# Revit family: Modular Panel_132X
name_source: partatom
category: Electrical Fixtures
revit_build: Autodesk Revit 2018 (Build: 20170223_1515(x64)
units: mm (PartAtom-declared; Revit-internal decimal feet)

## family parameters
Always vertical = Yes
Cut with Voids When Loaded = No
Maintain Annotation Orientation = No
Part Type = Normal
Room Calculation Point = No
Round Connector Dimension = Use Diameter
Shared = No
Work Plane-Based = Yes

## types (1)
- 2-Button Module Raise/Lower Black/White
    Ambient temperature = 0 °C to +40 °C
    Cable rating = All cables must be mains rated.
    DALI cable = Removable connector block ,Wire size: 0.5 mm² – 2.5 mm² solid or stranded
    DALI consumption = 10 mA
    DALI data transfer = All DIGIDIM modular panels use a data protocol that conforms to the DALI protocol.
    DALI supply input = 13 V to 22.5 V
    Default Elevation = 0 mm  [stored 0 ft]
    Dimensions: = 35.4 mm × 48.4 mm × 31.8 mm
    EMC emission = EN 55015
    EMC immunity = EN 61547
    Environment = Complies with WEEE and RoHS directives.
    IP code: = IP30
    IR frequency = 36 kHz
    Manufacturer = Helvar
    Model = 132W/132B
    Module Weight: = 41 g with DALI connector
    Relative humidity = Max. 90 %, noncondensing
    Safety = EN 61347-2-11
    Storage temperature = –10 °C to +70 °C

note: [stored X ft] marks values corroborated as IEEE doubles in the binary element streams (Revit-internal decimal feet)

## geometry (parser evidence)
native form markers: Sweep x5
no freeform markers — native parametric forms only
